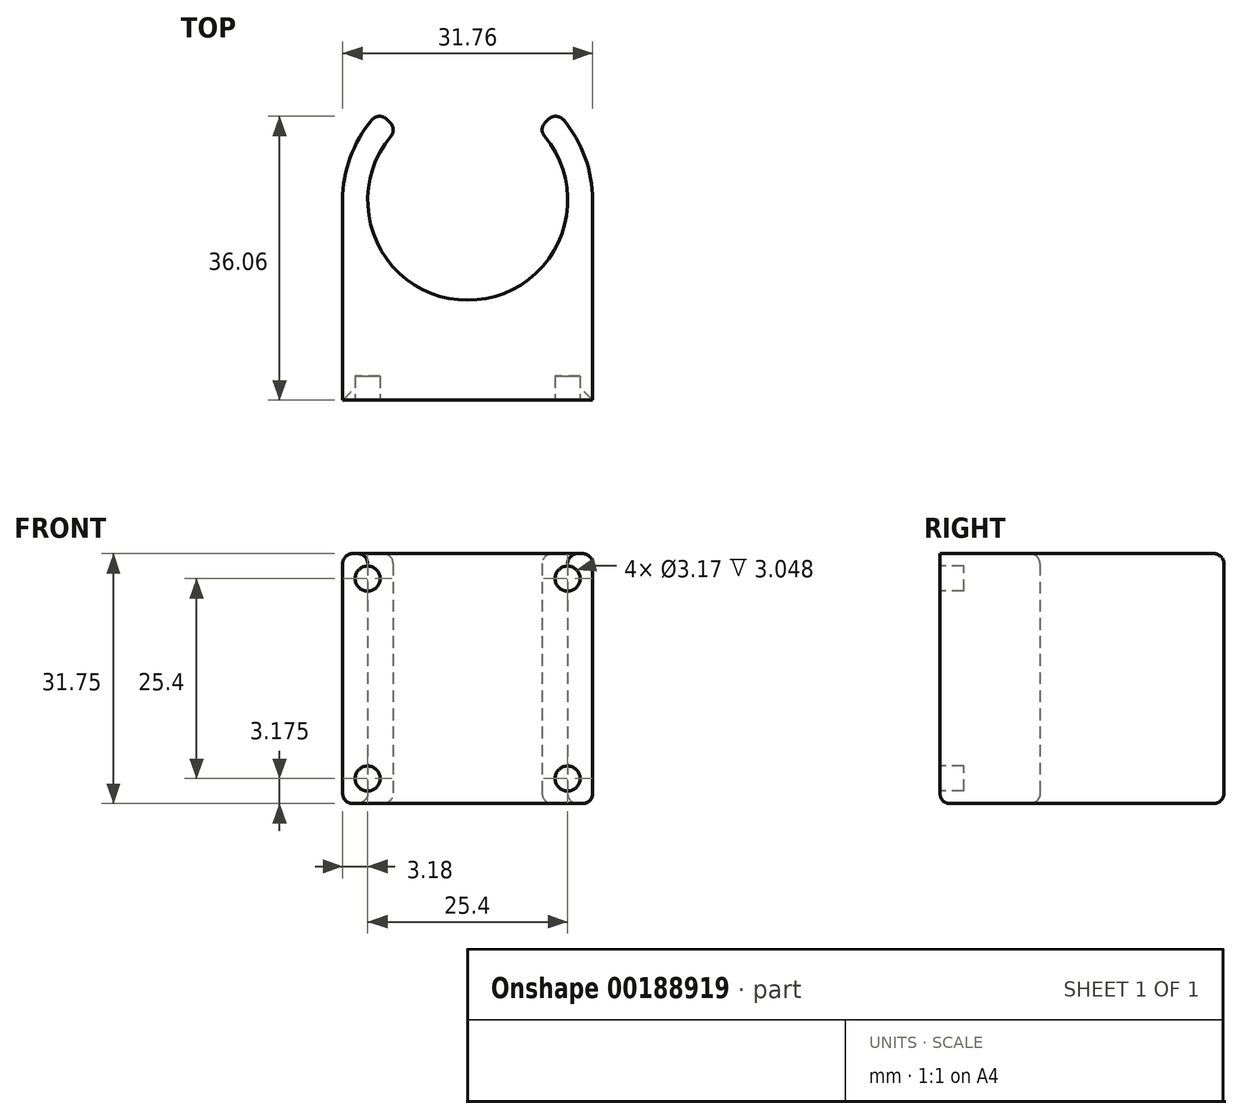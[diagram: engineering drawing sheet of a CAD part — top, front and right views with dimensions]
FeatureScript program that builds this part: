
annotation { "Feature Type Name" : "Feature", "Feature Type Description" : "" }
export const myFeature = defineFeature(function(context is Context, id is Id, definition is map)
    precondition{}
    {
        {
            var Q0;
            Q0=qCreatedBy(makeId("Top.planeOp"),FACE);
            var sketch = newSketch(context, id + "F0", { "sketchPlane" : qUnion([Q0])});
            skArc(sketch, "E0", {"start": v(-8.98, 8.98) * mm, "mid": v(0, -12.7) * mm, "end": v(8.98, 8.98) * mm});
            skArc(sketch, "E1", {"start": v(-11.23, 11.23) * mm, "mid": v(-14.67, 6.08) * mm, "end": v(-15.88, 0) * mm});
            skLineSegment(sketch, "E2", {"start": v(-15.88, 0) * mm, "end": v(-15.88, -25.4) * mm});
            skLineSegment(sketch, "E3", {"start": v(-15.88, -25.4) * mm, "end": v(15.88, -25.4) * mm});
            skLineSegment(sketch, "E4", {"start": v(15.88, -25.4) * mm, "end": v(15.88, 0) * mm});
            skLineSegment(sketch, "E5", {"start": v(-8.98, 8.98) * mm, "end": v(-11.23, 11.23) * mm});
            skLineSegment(sketch, "E6", {"start": v(11.23, 11.23) * mm, "end": v(8.98, 8.98) * mm});
            skArc(sketch, "E7.trimOffspring", {"start": v(15.88, 0) * mm, "mid": v(14.67, 6.08) * mm, "end": v(11.23, 11.23) * mm});
            skSolve(sketch);
        }
        {
            var Q0;
            Q0=qSketchRegion(id+"F0",true);
            extrude(context, id + "F1", {"entities" : qUnion([Q0]), "depth" : 31.75 * mm});
        }
        {
            var Q0;
            Q0=makeQuery(id+"F1.opExtrude","SWEPT_FACE",FACE,{"disambiguationData":[OSD([sQuery(id+"F0.wireOp",EDGE,"E3")])]});
            var sketch = newSketch(context, id + "F2", { "sketchPlane" : qUnion([Q0])});
            skCircle(sketch, "E8", {"center": v(-12.7, 28.57) * mm, "radius": 1.59 * mm});
            skCircle(sketch, "E9", {"center": v(12.7, 28.57) * mm, "radius": 1.59 * mm});
            skCircle(sketch, "E10", {"center": v(12.7, 3.18) * mm, "radius": 1.59 * mm});
            skCircle(sketch, "E11", {"center": v(-12.7, 3.18) * mm, "radius": 1.59 * mm});
            skLineSegment(sketch, "E12", {"start": v(-12.7, 28.57) * mm, "end": v(-12.7, 3.18) * mm, "construction": true});
            skLineSegment(sketch, "E13", {"start": v(12.7, 3.18) * mm, "end": v(12.7, 28.57) * mm, "construction": true});
            skLineSegment(sketch, "E14", {"start": v(-12.7, 28.57) * mm, "end": v(12.7, 28.57) * mm, "construction": true});
            skLineSegment(sketch, "E15", {"start": v(-12.7, 3.18) * mm, "end": v(12.7, 3.18) * mm, "construction": true});
            skLineSegment(sketch, "E16", {"start": v(0, 0) * mm, "end": v(0, 3.18) * mm, "construction": true});
            skLineSegment(sketch, "E17", {"start": v(-15.88, 15.88) * mm, "end": v(-12.7, 15.88) * mm, "construction": true});
            skSolve(sketch);
        }
        {
            var Q0;
            Q0=qSketchRegion(id+"F2",true);
            extrude(context, id + "F3", {"entities" : qUnion([Q0]), "operationType" : NewBodyOperationType.REMOVE, "oppositeDirection" : true, "depth" : 3.05 * mm});
        }
        {
            var Q0;
            Q0=makeQuery(id+"F1.opExtrude","CAP_EDGE",EDGE,{"disambiguationData":[OSD([sQuery(id+"F0.wireOp",EDGE,"E2")])],"isStart":false});
            var Q1;
            Q1=makeQuery(id+"F1.opExtrude","CAP_EDGE",EDGE,{"disambiguationData":[OSD([sQuery(id+"F0.wireOp",EDGE,"E0")])],"isStart":false});
            var Q2;
            Q2=makeQuery(id+"F1.opExtrude","CAP_EDGE",EDGE,{"disambiguationData":[OSD([sQuery(id+"F0.wireOp",EDGE,"E4")])],"isStart":false});
            var Q3;
            Q3=makeQuery(id+"F1.opExtrude","CAP_FACE",FACE,{"disambiguationData":[OSD([sQuery(id+"F0.wireOp",EDGE,"E0"),sQuery(id+"F0.wireOp",EDGE,"E1"),sQuery(id+"F0.wireOp",EDGE,"E2"),sQuery(id+"F0.wireOp",EDGE,"E3"),sQuery(id+"F0.wireOp",EDGE,"E4"),sQuery(id+"F0.wireOp",EDGE,"E5"),sQuery(id+"F0.wireOp",EDGE,"E6"),sQuery(id+"F0.wireOp",EDGE,"E7.trimOffspring")])],"isStart":true});
            var Q4;
            Q4=makeQuery(id+"F1.opExtrude","SWEPT_FACE",FACE,{"disambiguationData":[OSD([sQuery(id+"F0.wireOp",EDGE,"E5")])]});
            var Q5;
            Q5=makeQuery(id+"F1.opExtrude","SWEPT_FACE",FACE,{"disambiguationData":[OSD([sQuery(id+"F0.wireOp",EDGE,"E6")])]});
            fillet(context, id + "F4", {"entities" : qUnion([Q0, Q1, Q2, Q3, Q4, Q5]), "radius" : 1.27 * mm, "tangentPropagation" : true, "allowEdgeOverflow" : false});
        }
    });
